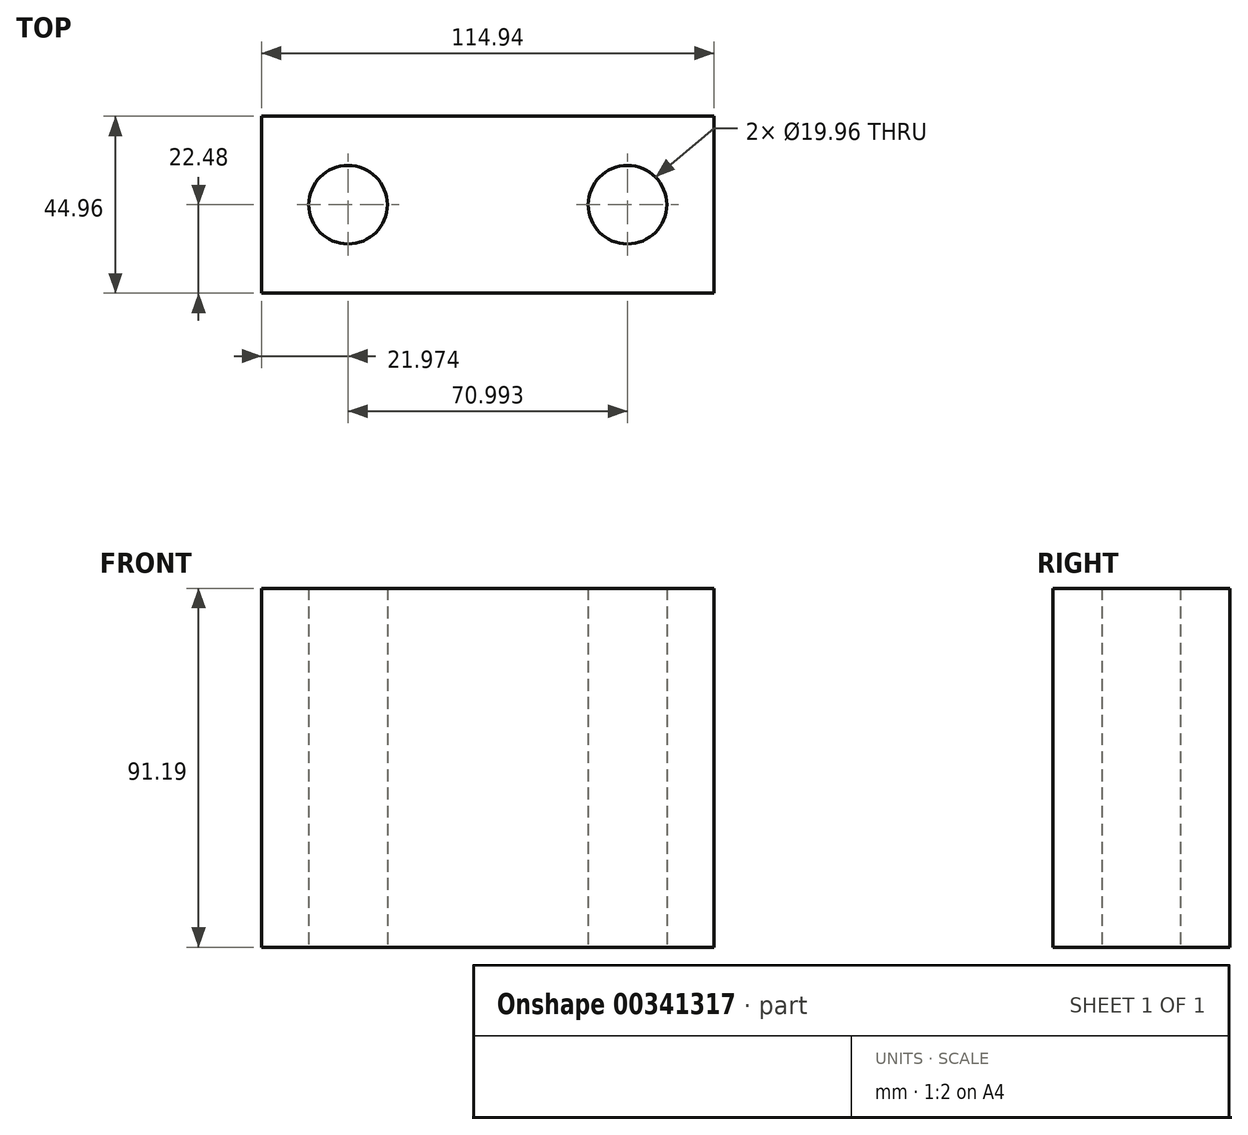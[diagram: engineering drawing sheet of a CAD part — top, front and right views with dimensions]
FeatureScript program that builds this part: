
annotation { "Feature Type Name" : "Feature", "Feature Type Description" : "" }
export const myFeature = defineFeature(function(context is Context, id is Id, definition is map)
    precondition{}
    {
        {
            var Q0;
            Q0=qCreatedBy(makeId("Top.planeOp"),FACE);
            var sketch = newSketch(context, id + "F0", { "sketchPlane" : qUnion([Q0])});
            skLineSegment(sketch, "E0.bottom", {"start": v(57.47, 22.48) * mm, "end": v(-57.47, 22.48) * mm});
            skLineSegment(sketch, "E0.top", {"start": v(57.47, -22.48) * mm, "end": v(-57.47, -22.48) * mm});
            skLineSegment(sketch, "E0.left", {"start": v(57.47, 22.48) * mm, "end": v(57.47, -22.48) * mm});
            skLineSegment(sketch, "E0.right", {"start": v(-57.47, 22.48) * mm, "end": v(-57.47, -22.48) * mm});
            skPoint(sketch, "E0.middle", {"position": v(0, 0) * mm});
            skCircle(sketch, "E1", {"center": v(-35.5, 0) * mm, "radius": 9.98 * mm});
            skCircle(sketch, "E2", {"center": v(35.5, 0) * mm, "radius": 9.98 * mm});
            skSolve(sketch);
        }
        {
            var Q0;
            Q0 = qSketchRegion(id + "F0", true);
            extrude(context, id + "F1", {"entities" : qUnion([Q0]), "depth" : 91.19 * mm});
        }
    });
